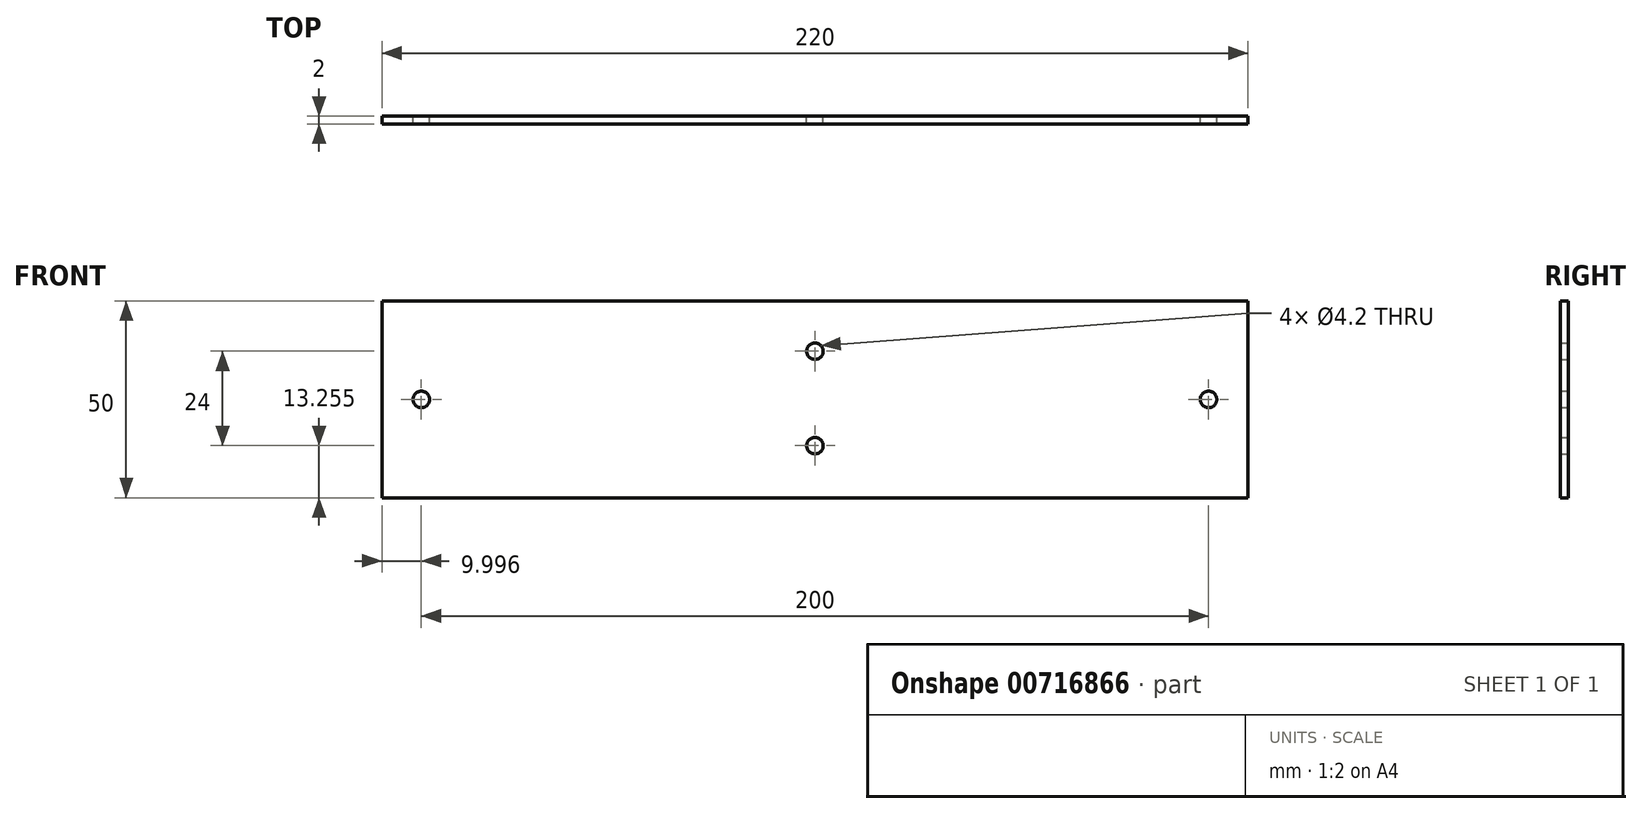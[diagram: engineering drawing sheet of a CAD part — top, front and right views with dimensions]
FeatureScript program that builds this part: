
annotation { "Feature Type Name" : "Feature", "Feature Type Description" : "" }
export const myFeature = defineFeature(function(context is Context, id is Id, definition is map)
    precondition{}
    {
        {
            var Q0;
            Q0=qCreatedBy(makeId("Front.planeOp"),FACE);
            var sketch = newSketch(context, id + "F0", { "sketchPlane" : qUnion([Q0])});
            skLineSegment(sketch, "E0.bottom", {"start": v(-0.2, 49.83) * mm, "end": v(219.8, 49.83) * mm});
            skLineSegment(sketch, "E0.top", {"start": v(-0.2, -0.17) * mm, "end": v(219.8, -0.17) * mm});
            skLineSegment(sketch, "E0.left", {"start": v(-0.2, 49.83) * mm, "end": v(-0.2, -0.17) * mm});
            skLineSegment(sketch, "E0.right", {"start": v(219.8, 49.83) * mm, "end": v(219.8, -0.17) * mm});
            skPoint(sketch, "E1.centerSnap0", {"position": v(-0.2, 24.83) * mm});
            skCircle(sketch, "E2", {"center": v(9.8, 24.83) * mm, "radius": 2.1 * mm});
            skCircle(sketch, "E3", {"center": v(109.8, 37.09) * mm, "radius": 2.1 * mm});
            skCircle(sketch, "E4", {"center": v(209.8, 24.83) * mm, "radius": 2.1 * mm});
            skLineSegment(sketch, "E5", {"start": v(109.8, 37.09) * mm, "end": v(109.8, 13.09) * mm});
            skCircle(sketch, "E6", {"center": v(109.8, 13.09) * mm, "radius": 2.1 * mm});
            skSolve(sketch);
        }
        {
            var Q0;
            Q0=makeQuery(id+"F0.imprint","IMPRINT",FACE,{"disambiguationData":[TD([[makeQuery(id+"F0.imprint","IMPRINT",EDGE,{"derivedFrom":sQuery(id+"F0.wireOp",EDGE,"E0.bottom")}),-1.0]])]});
            extrude(context, id + "F1", {"entities" : qUnion([Q0]), "depth" : 2 * mm, "offsetDistance" : 25 * mm});
        }
    });
